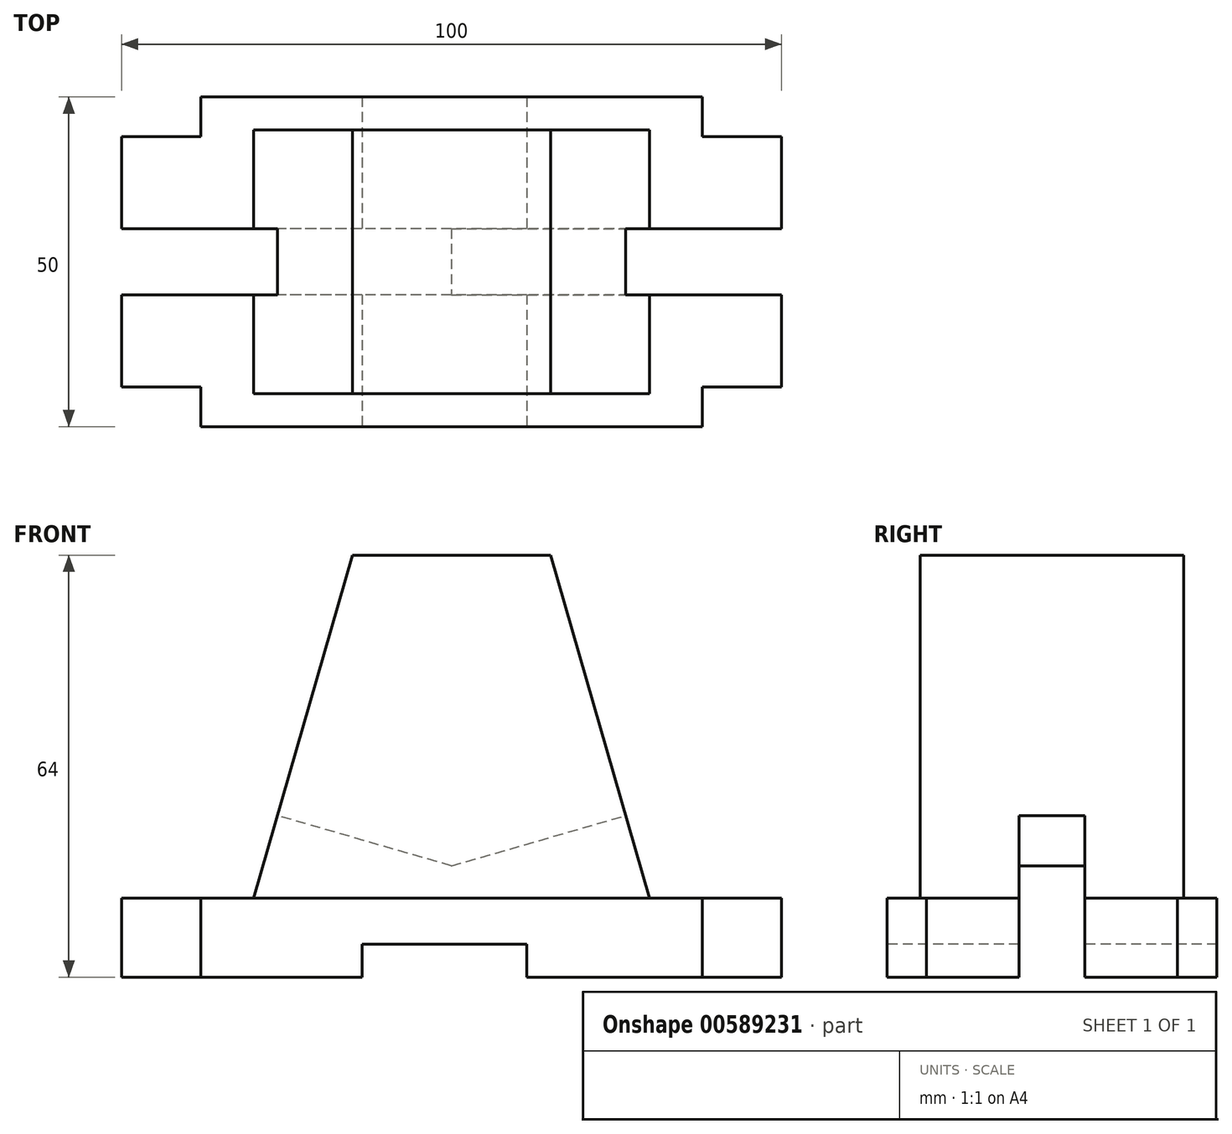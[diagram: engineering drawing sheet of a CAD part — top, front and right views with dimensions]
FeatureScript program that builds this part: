
annotation { "Feature Type Name" : "Feature", "Feature Type Description" : "" }
export const myFeature = defineFeature(function(context is Context, id is Id, definition is map)
    precondition{}
    {
        {
            var Q0;
            Q0=qCreatedBy(makeId("Front.planeOp"),FACE);
            var sketch = newSketch(context, id + "F0", { "sketchPlane" : qUnion([Q0])});
            skLineSegment(sketch, "E0", {"start": v(-47.74, -42.78) * mm, "end": v(52.26, -42.78) * mm});
            skLineSegment(sketch, "E1", {"start": v(-47.74, -42.78) * mm, "end": v(-47.74, -30.78) * mm});
            skLineSegment(sketch, "E2", {"start": v(-47.74, -30.78) * mm, "end": v(52.26, -30.78) * mm});
            skLineSegment(sketch, "E3", {"start": v(52.26, -30.78) * mm, "end": v(52.26, -42.78) * mm});
            skSolve(sketch);
        }
        {
            var Q0;
            Q0 = qSketchRegion(id + "F0", true);
            extrude(context, id + "F1", {"entities" : qUnion([Q0]), "oppositeDirection" : true, "depth" : 50 * mm, "offsetDistance" : 25 * mm});
        }
        {
            var Q0;
            Q0=makeQuery(id+"F1.opExtrude","CAP_FACE",FACE,{"disambiguationData":[OSD([sQuery(id+"F0.wireOp",EDGE,"E0"),sQuery(id+"F0.wireOp",EDGE,"E1"),sQuery(id+"F0.wireOp",EDGE,"E2"),sQuery(id+"F0.wireOp",EDGE,"E3")])],"isStart":true});
            var sketch = newSketch(context, id + "F2", { "sketchPlane" : qUnion([Q0])});
            skLineSegment(sketch, "E4", {"start": v(2.26, -24.1) * mm, "end": v(2.26, -74.83) * mm, "construction": true});
            skPoint(sketch, "E4.startSnap0", {"position": v(2.26, -30.78) * mm});
            skPoint(sketch, "E4.endSnap0", {"position": v(2.26, -42.78) * mm});
            skLineSegment(sketch, "E5", {"start": v(2.26, -42.78) * mm, "end": v(-11.31, -42.78) * mm});
            skLineSegment(sketch, "E6", {"start": v(-11.31, -42.78) * mm, "end": v(-11.31, -37.78) * mm});
            skLineSegment(sketch, "E7", {"start": v(-11.31, -37.78) * mm, "end": v(13.69, -37.78) * mm});
            skLineSegment(sketch, "E8", {"start": v(13.69, -37.78) * mm, "end": v(13.69, -42.78) * mm});
            skLineSegment(sketch, "E9", {"start": v(13.69, -42.78) * mm, "end": v(2.26, -42.78) * mm});
            skSolve(sketch);
        }
        {
            var Q0;
            Q0=makeQuery(id+"F2.imprint","IMPRINT",FACE,{"disambiguationData":[TD([[makeQuery(id+"F2.imprint","IMPRINT",EDGE,{"derivedFrom":sQuery(id+"F2.wireOp",EDGE,"E5")}),1.0]])]});
            extrude(context, id + "F3", {"entities" : qUnion([Q0]), "operationType" : NewBodyOperationType.REMOVE, "endBound" : BoundingType.THROUGH_ALL, "oppositeDirection" : true, "depth" : 25 * mm, "offsetDistance" : 25 * mm});
        }
        {
            var Q0;
            Q0=makeQuery(id+"F1.opExtrude","SWEPT_FACE",FACE,{"disambiguationData":[OSD([sQuery(id+"F0.wireOp",EDGE,"E2")])]});
            var sketch = newSketch(context, id + "F4", { "sketchPlane" : qUnion([Q0])});
            skLineSegment(sketch, "E10", {"start": v(-47.74, 0) * mm, "end": v(-47.74, 6) * mm});
            skLineSegment(sketch, "E11", {"start": v(-47.74, 6) * mm, "end": v(-35.74, 6) * mm});
            skLineSegment(sketch, "E12", {"start": v(-35.74, 6) * mm, "end": v(-35.74, 0) * mm});
            skLineSegment(sketch, "E13", {"start": v(-35.74, 0) * mm, "end": v(-47.74, 0) * mm});
            skLineSegment(sketch, "E14", {"start": v(-62.2, 25) * mm, "end": v(83.38, 25) * mm, "construction": true});
            skPoint(sketch, "E14.startSnap0", {"position": v(-47.74, 25) * mm});
            skLineSegment(sketch, "E15", {"start": v(-47.74, 25) * mm, "end": v(-47.74, 20) * mm});
            skLineSegment(sketch, "E16.MirrorCS", {"start": v(-47.74, 25) * mm, "end": v(-47.74, 30) * mm});
            skLineSegment(sketch, "E17", {"start": v(52.26, 30) * mm, "end": v(52.26, 20) * mm});
            skLineSegment(sketch, "E18.MirrorCS", {"start": v(-47.74, 44) * mm, "end": v(-35.74, 44) * mm});
            skLineSegment(sketch, "E19.MirrorCS", {"start": v(-35.74, 44) * mm, "end": v(-35.74, 50) * mm});
            skLineSegment(sketch, "E20.MirrorCS", {"start": v(-35.74, 50) * mm, "end": v(-47.74, 50) * mm});
            skLineSegment(sketch, "E21.MirrorCS", {"start": v(-47.74, 50) * mm, "end": v(-47.74, 44) * mm});
            skLineSegment(sketch, "E22", {"start": v(2.26, 60.47) * mm, "end": v(2.26, -14.42) * mm, "construction": true});
            skPoint(sketch, "E22.startSnap0", {"position": v(2.26, 50) * mm});
            skLineSegment(sketch, "E23.MirrorCS", {"start": v(40.26, 44) * mm, "end": v(40.26, 50) * mm});
            skLineSegment(sketch, "E24.MirrorCS", {"start": v(40.26, 50) * mm, "end": v(52.26, 50) * mm});
            skLineSegment(sketch, "E25.MirrorCS", {"start": v(52.26, 50) * mm, "end": v(52.26, 44) * mm});
            skLineSegment(sketch, "E26.MirrorCS", {"start": v(52.26, 44) * mm, "end": v(40.26, 44) * mm});
            skLineSegment(sketch, "E27.MirrorCS", {"start": v(52.26, 6) * mm, "end": v(40.26, 6) * mm});
            skLineSegment(sketch, "E28.MirrorCS", {"start": v(40.26, 0) * mm, "end": v(52.26, 0) * mm});
            skLineSegment(sketch, "E29.MirrorCS", {"start": v(40.26, 6) * mm, "end": v(40.26, 0) * mm});
            skLineSegment(sketch, "E30.MirrorCS", {"start": v(52.26, 0) * mm, "end": v(52.26, 6) * mm});
            skSolve(sketch);
        }
        {
            var Q0;
            Q0 = qSketchRegion(id + "F4", true);
            extrude(context, id + "F5", {"entities" : qUnion([Q0]), "operationType" : NewBodyOperationType.REMOVE, "endBound" : BoundingType.THROUGH_ALL, "oppositeDirection" : true, "depth" : 25 * mm, "offsetDistance" : 25 * mm});
        }
        {
            var Q0;
            Q0=makeQuery(id+"F1.opExtrude","SWEPT_FACE",FACE,{"disambiguationData":[OSD([sQuery(id+"F0.wireOp",EDGE,"E2")])]});
            var sketch = newSketch(context, id + "F6", { "sketchPlane" : qUnion([Q0])});
            skLineSegment(sketch, "E31", {"start": v(32.26, -11.12) * mm, "end": v(32.26, 73.2) * mm, "construction": true});
            skLineSegment(sketch, "E32", {"start": v(-55.11, 25) * mm, "end": v(78.43, 25) * mm, "construction": true});
            skPoint(sketch, "E32.startSnap0", {"position": v(-47.74, 25) * mm});
            skLineSegment(sketch, "E33", {"start": v(32.26, 25) * mm, "end": v(32.26, 5) * mm});
            skLineSegment(sketch, "E34", {"start": v(32.26, 5) * mm, "end": v(-27.74, 5) * mm});
            skLineSegment(sketch, "E35", {"start": v(-27.74, 5) * mm, "end": v(-27.74, 45) * mm});
            skLineSegment(sketch, "E36", {"start": v(-27.74, 45) * mm, "end": v(32.26, 45) * mm});
            skPoint(sketch, "E36.endSnap0", {"position": v(32.26, 31.05) * mm});
            skLineSegment(sketch, "E37", {"start": v(32.26, 45) * mm, "end": v(32.26, 25) * mm});
            skSolve(sketch);
        }
        {
            var Q0;
            Q0 = qSketchRegion(id + "F6", true);
            extrude(context, id + "F7", {"entities" : qUnion([Q0]), "operationType" : NewBodyOperationType.ADD, "depth" : 52 * mm, "offsetDistance" : 25 * mm});
        }
        {
            var Q0;
            Q0=makeQuery(id+"F7.opExtrude","SWEPT_FACE",FACE,{"disambiguationData":[OSD([sQuery(id+"F6.wireOp",EDGE,"E34")])]});
            cPlane(context, id + "F8", {"entities" : qUnion([Q0]), "cplaneType" : CPlaneType.OFFSET, "offset" : 0 * mm, "oppositeDirection" : true, "width" : 150 * mm, "height" : 150 * mm});
        }
        {
            var Q0;
            Q0=qCreatedBy(id+"F8.planeOp",FACE);
            var sketch = newSketch(context, id + "F9", { "sketchPlane" : qUnion([Q0])});
            skLineSegment(sketch, "E38", {"start": v(2.26, 26.45) * mm, "end": v(2.26, -45.6) * mm, "construction": true});
            skPoint(sketch, "E38.startSnap0", {"position": v(2.26, 21.22) * mm});
            skLineSegment(sketch, "E39", {"start": v(-12.74, 21.22) * mm, "end": v(17.26, 21.22) * mm});
            skLineSegment(sketch, "E40", {"start": v(-12.74, 21.22) * mm, "end": v(-27.74, -30.78) * mm});
            skLineSegment(sketch, "E41", {"start": v(-27.74, -30.78) * mm, "end": v(-27.74, 21.23) * mm});
            skLineSegment(sketch, "E42", {"start": v(-12.74, 21.22) * mm, "end": v(-27.74, 21.23) * mm});
            skLineSegment(sketch, "E43.MirrorCS", {"start": v(17.26, 21.22) * mm, "end": v(32.26, -30.78) * mm});
            skLineSegment(sketch, "E44.MirrorCS", {"start": v(17.26, 21.22) * mm, "end": v(32.26, 21.23) * mm});
            skLineSegment(sketch, "E45.MirrorCS", {"start": v(32.26, -30.78) * mm, "end": v(32.26, 21.23) * mm});
            skSolve(sketch);
        }
        {
            var Q0;
            Q0=makeQuery(id+"F9.imprint","IMPRINT",FACE,{"disambiguationData":[TD([[makeQuery(id+"F9.imprint","IMPRINT",EDGE,{"derivedFrom":sQuery(id+"F9.wireOp",EDGE,"E40")}),-1.0]])]});
            var Q1;
            Q1=makeQuery(id+"F9.imprint","IMPRINT",FACE,{"disambiguationData":[TD([[makeQuery(id+"F9.imprint","IMPRINT",EDGE,{"derivedFrom":sQuery(id+"F9.wireOp",EDGE,"E43.MirrorCS")}),1.0]])]});
            extrude(context, id + "F10", {"entities" : qUnion([Q0, Q1]), "operationType" : NewBodyOperationType.REMOVE, "endBound" : BoundingType.THROUGH_ALL, "oppositeDirection" : true, "depth" : 25 * mm, "offsetDistance" : 25 * mm});
        }
        {
            var Q0;
            Q0=makeQuery(id+"F7.opExtrude","SWEPT_FACE",FACE,{"disambiguationData":[OSD([sQuery(id+"F6.wireOp",EDGE,"E34")])]});
            var sketch = newSketch(context, id + "F11", { "sketchPlane" : qUnion([Q0])});
            skLineSegment(sketch, "E46", {"start": v(2.04, 23.82) * mm, "end": v(2.04, -48.65) * mm, "construction": true});
            skPoint(sketch, "E46.startSnap0", {"position": v(2.04, 21.22) * mm});
            skLineSegment(sketch, "E47", {"start": v(2.04, 21.22) * mm, "end": v(-5.46, 21.22) * mm});
            skLineSegment(sketch, "E48.MirrorCS", {"start": v(2.04, 21.22) * mm, "end": v(9.54, 21.22) * mm});
            skLineSegment(sketch, "E49", {"start": v(-5.46, 21.22) * mm, "end": v(-5.46, 1.22) * mm});
            skLineSegment(sketch, "E50", {"start": v(-5.46, 1.22) * mm, "end": v(2.04, 1.22) * mm});
            skLineSegment(sketch, "E51.MirrorCS", {"start": v(9.54, 21.22) * mm, "end": v(9.54, 1.22) * mm});
            skLineSegment(sketch, "E52.MirrorCS", {"start": v(9.54, 1.22) * mm, "end": v(2.04, 1.22) * mm});
            skSolve(sketch);
        }
        {
            var Q0;
            Q0=makeQuery(id+"F11.imprint","IMPRINT",FACE,{"disambiguationData":[TD([[makeQuery(id+"F11.imprint","IMPRINT",EDGE,{"derivedFrom":sQuery(id+"F11.wireOp",EDGE,"E47")}),1.0]])]});
            extrude(context, id + "F12", {"entities" : qUnion([Q0]), "operationType" : NewBodyOperationType.REMOVE, "endBound" : BoundingType.THROUGH_ALL, "oppositeDirection" : true, "depth" : 25 * mm, "offsetDistance" : 25 * mm});
        }
        {
            var Q0;
            Q0=makeQuery(id+"F1.opExtrude","SWEPT_FACE",FACE,{"disambiguationData":[OSD([sQuery(id+"F0.wireOp",EDGE,"E1")])]});
            var sketch = newSketch(context, id + "F13", { "sketchPlane" : qUnion([Q0])});
            skLineSegment(sketch, "E53", {"start": v(-25, -42.78) * mm, "end": v(-30, -42.78) * mm});
            skLineSegment(sketch, "E54", {"start": v(-25, -42.78) * mm, "end": v(-20, -42.78) * mm});
            skLineSegment(sketch, "E55", {"start": v(-20, -42.78) * mm, "end": v(-20, -30.78) * mm});
            skLineSegment(sketch, "E56", {"start": v(-30, -42.78) * mm, "end": v(-30, -30.78) * mm});
            skSolve(sketch);
        }
        {
            var Q0;
            Q0=makeQuery(id+"F13.imprint","IMPRINT",FACE,{"disambiguationData":[TD([[makeQuery(id+"F13.imprint","IMPRINT",EDGE,{"derivedFrom":sQuery(id+"F13.wireOp",EDGE,"E53")}),1.0]])]});
            extrude(context, id + "F14", {"entities" : qUnion([Q0]), "operationType" : NewBodyOperationType.REMOVE, "endBound" : BoundingType.THROUGH_ALL, "oppositeDirection" : true, "depth" : 25 * mm, "offsetDistance" : 25 * mm});
        }
        {
            var Q0;
            Q0=makeQuery(id+"F10.boolean.opBoolean","COPY",FACE,{"derivedFrom":makeQuery(id+"F10.opExtrude","SWEPT_FACE",FACE,{"disambiguationData":[OSD([sQuery(id+"F9.wireOp",EDGE,"E40")])]})});
            cPlane(context, id + "F15", {"entities" : qUnion([Q0]), "cplaneType" : CPlaneType.OFFSET, "offset" : 25 * mm, "width" : 150 * mm, "height" : 150 * mm});
        }
        {
            var Q0;
            Q0=qCreatedBy(id+"F15.planeOp",FACE);
            var sketch = newSketch(context, id + "F16", { "sketchPlane" : qUnion([Q0])});
            skLineSegment(sketch, "E57", {"start": v(-30, -37.26) * mm, "end": v(-30, -24.26) * mm});
            skLineSegment(sketch, "E58", {"start": v(-20, -37.26) * mm, "end": v(-20, -24.26) * mm});
            skLineSegment(sketch, "E59", {"start": v(-30, -24.26) * mm, "end": v(-20, -24.26) * mm});
            skLineSegment(sketch, "E60", {"start": v(-30, -37.26) * mm, "end": v(-20, -37.26) * mm});
            skSolve(sketch);
        }
        {
            var Q0;
            Q0 = qSketchRegion(id + "F16", true);
            extrude(context, id + "F17", {"entities" : qUnion([Q0]), "operationType" : NewBodyOperationType.REMOVE, "endBound" : BoundingType.THROUGH_ALL, "oppositeDirection" : true, "depth" : 25 * mm, "offsetDistance" : 25 * mm});
        }
        {
            var Q0;
            Q0=makeQuery(id+"F10.boolean.opBoolean","COPY",FACE,{"derivedFrom":makeQuery(id+"F10.opExtrude","SWEPT_FACE",FACE,{"disambiguationData":[OSD([sQuery(id+"F9.wireOp",EDGE,"E43.MirrorCS")])]})});
            cPlane(context, id + "F18", {"entities" : qUnion([Q0]), "cplaneType" : CPlaneType.OFFSET, "offset" : 25 * mm, "width" : 150 * mm, "height" : 150 * mm});
        }
        {
            var Q0;
            Q0=qCreatedBy(id+"F18.planeOp",FACE);
            var sketch = newSketch(context, id + "F19", { "sketchPlane" : qUnion([Q0])});
            skLineSegment(sketch, "E61", {"start": v(20, -38.51) * mm, "end": v(20, -25.51) * mm});
            skLineSegment(sketch, "E62", {"start": v(30, -38.51) * mm, "end": v(30, -25.51) * mm});
            skLineSegment(sketch, "E63", {"start": v(20, -25.51) * mm, "end": v(30, -25.51) * mm});
            skLineSegment(sketch, "E64", {"start": v(20, -38.51) * mm, "end": v(30, -38.51) * mm});
            skSolve(sketch);
        }
        {
            var Q0;
            Q0=makeQuery(id+"F19.imprint","IMPRINT",FACE,{"disambiguationData":[TD([[makeQuery(id+"F19.imprint","IMPRINT",EDGE,{"derivedFrom":sQuery(id+"F19.wireOp",EDGE,"E61")}),-1.0]])]});
            extrude(context, id + "F20", {"entities" : qUnion([Q0]), "operationType" : NewBodyOperationType.REMOVE, "endBound" : BoundingType.THROUGH_ALL, "oppositeDirection" : true, "depth" : 25 * mm, "offsetDistance" : 25 * mm});
        }
    });
